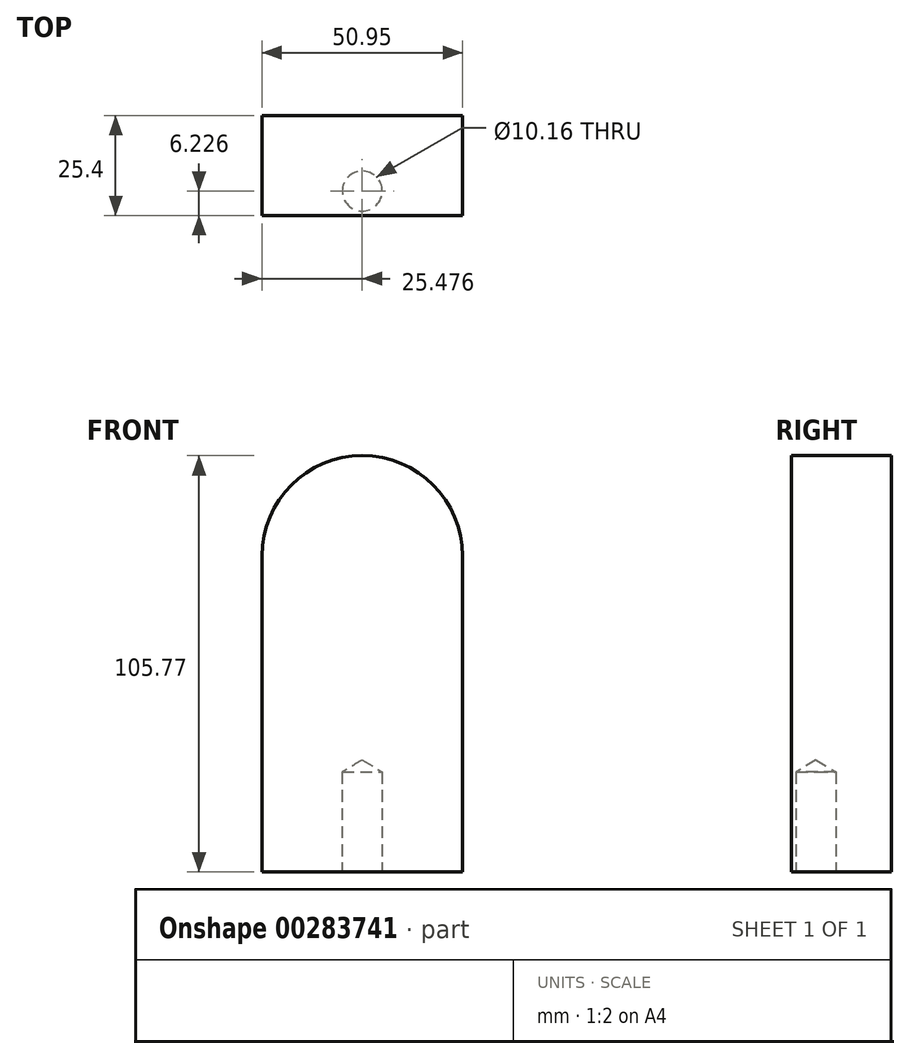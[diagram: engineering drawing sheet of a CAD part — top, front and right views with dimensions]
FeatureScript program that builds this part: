
annotation { "Feature Type Name" : "Feature", "Feature Type Description" : "" }
export const myFeature = defineFeature(function(context is Context, id is Id, definition is map)
    precondition{}
    {
        {
            var Q0;
            Q0=qCreatedBy(makeId("Front.planeOp"),FACE);
            var sketch = newSketch(context, id + "F0", { "sketchPlane" : qUnion([Q0])});
            skLineSegment(sketch, "E0.bottom", {"start": v(-19, 31.95) * mm, "end": v(31.95, 31.95) * mm});
            skLineSegment(sketch, "E0.top", {"start": v(-19, -48.35) * mm, "end": v(31.95, -48.35) * mm});
            skLineSegment(sketch, "E0.left", {"start": v(-19, 31.95) * mm, "end": v(-19, -48.35) * mm});
            skLineSegment(sketch, "E0.right", {"start": v(31.95, 31.95) * mm, "end": v(31.95, -48.35) * mm});
            skArc(sketch, "E1", {"start": v(-19, 31.95) * mm, "mid": v(6.48, 57.42) * mm, "end": v(31.95, 31.95) * mm});
            skSolve(sketch);
        }
        {
            var Q0;
            Q0 = qSketchRegion(id + "F0", true);
            extrude(context, id + "F1", {"entities" : qUnion([Q0]), "depth" : 25.4 * mm});
        }
        {
            var Q0;
            Q0=makeQuery(id+"F1.opExtrude","SWEPT_FACE",FACE,{"disambiguationData":[OSD([sQuery(id+"F0.wireOp",EDGE,"E0.top")])]});
            var sketch = newSketch(context, id + "F2", { "sketchPlane" : qUnion([Q0])});
            skCircle(sketch, "E2", {"center": v(6.48, 19.17) * mm, "radius": 3.54 * mm});
            skPoint(sketch, "E2.centerSnap0", {"position": v(6.48, 25.4) * mm});
            skSolve(sketch);
        }
        {
            var Q0;
            Q0=sQuery(id+"F2.wireOp",VERTEX,"E2.center");
            var Q1;
            Q1=makeQuery(id+"F1.opExtrude","SWEPT_BODY",BODY,{"disambiguationData":[OSD([sQuery(id+"F0.wireOp",EDGE,"E0.top"),sQuery(id+"F0.wireOp",EDGE,"E0.left"),sQuery(id+"F0.wireOp",EDGE,"E0.right"),sQuery(id+"F0.wireOp",EDGE,"E1")])]});
            hole(context, id + "F3", {"style" : HoleStyle.SIMPLE, "endStyle" : HoleEndStyle.BLIND, "holeDiameter" : 10.16 * mm, "holeDepth" : 25.4 * mm, "tappedDepth" : 12.7 * mm, "tapClearance" : 3, "locations" : qUnion([Q0]), "scope" : qUnion([Q1])});
        }
    });
